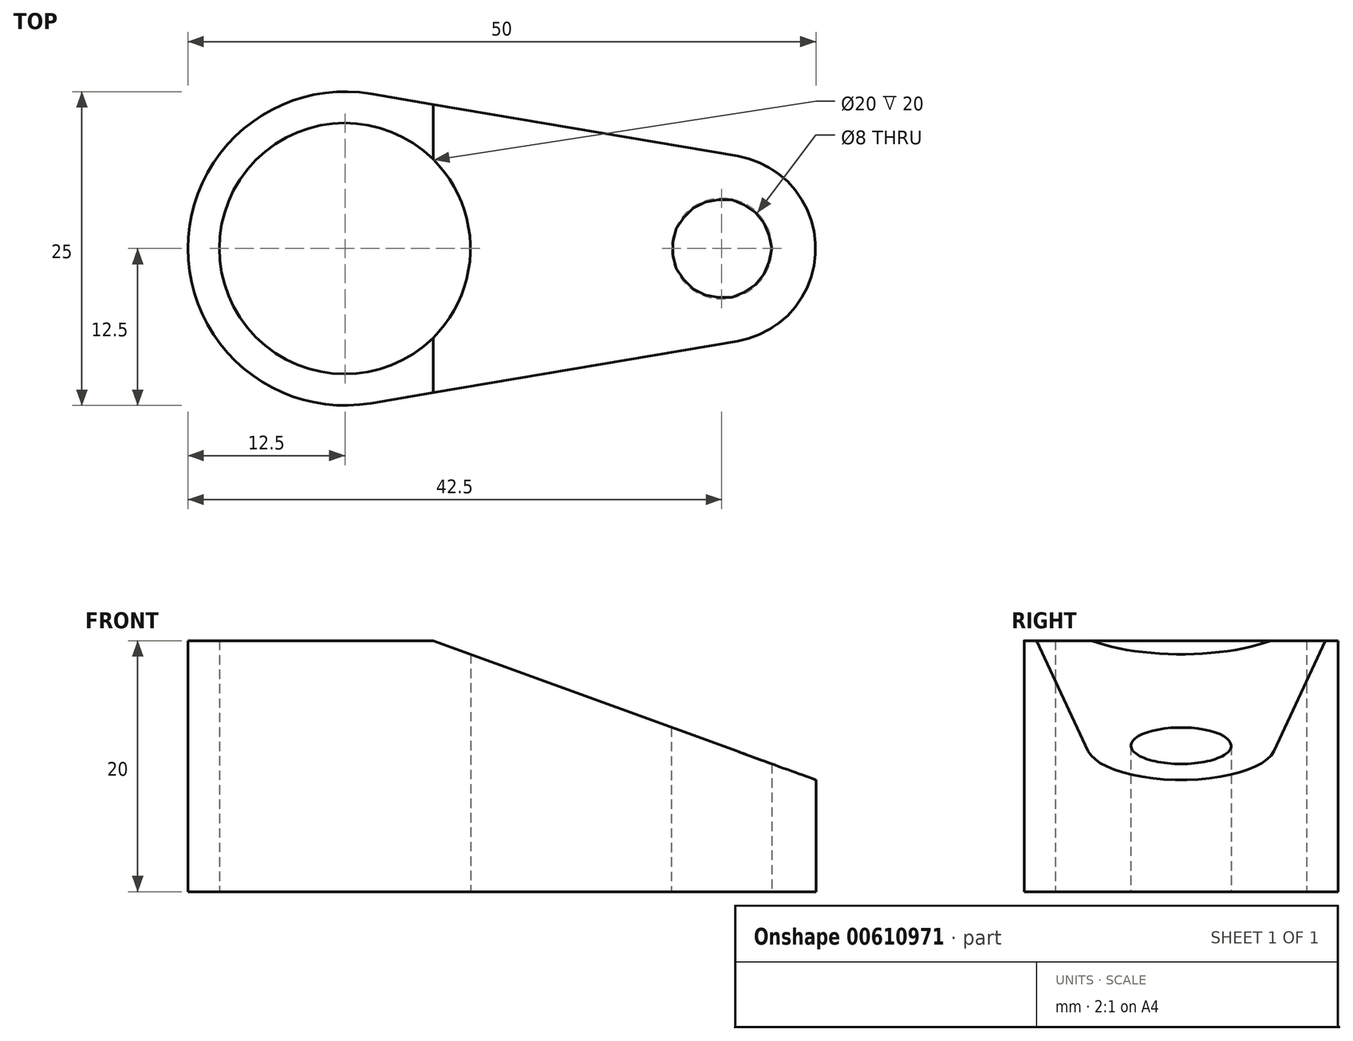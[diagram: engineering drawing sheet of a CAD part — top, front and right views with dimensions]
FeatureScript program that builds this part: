
annotation { "Feature Type Name" : "Feature", "Feature Type Description" : "" }
export const myFeature = defineFeature(function(context is Context, id is Id, definition is map)
    precondition{}
    {
        {
            var Q0;
            Q0=qCreatedBy(makeId("Top.planeOp"),FACE);
            var sketch = newSketch(context, id + "F0", { "sketchPlane" : qUnion([Q0])});
            skCircle(sketch, "E0", {"center": v(0, 0) * mm, "radius": 12.5 * mm});
            skCircle(sketch, "E1", {"center": v(30, 0) * mm, "radius": 7.5 * mm});
            skCircle(sketch, "E2", {"center": v(0, 0) * mm, "radius": 10 * mm});
            skCircle(sketch, "E3", {"center": v(30, 0) * mm, "radius": 4 * mm});
            skLineSegment(sketch, "E4", {"start": v(2.08, -12.33) * mm, "end": v(31.25, -7.4) * mm});
            skLineSegment(sketch, "E5", {"start": v(2.08, 12.33) * mm, "end": v(31.25, 7.4) * mm});
            skSolve(sketch);
        }
        {
            var Q0;
            Q0=makeQuery(id+"F0.imprint","IMPRINT",FACE,{"disambiguationData":[TD([[makeQuery(id+"F0.imprint","IMPRINT",EDGE,{"derivedFrom":sQuery(id+"F0.wireOp",EDGE,"E2")}),-1.0]])]});
            var Q1;
            Q1=makeQuery(id+"F0.imprint","IMPRINT",FACE,{"disambiguationData":[TD([[makeQuery(id+"F0.imprint","IMPRINT",EDGE,{"derivedFrom":sQuery(id+"F0.wireOp",EDGE,"E3")}),-1.0]])]});
            var Q2;
            {var subQ0=sQuery(id+"F0.wireOp",EDGE,"E4");Q2=makeQuery(id+"F0.imprint","IMPRINT",FACE,{"disambiguationData":[TD([[makeQuery(id+"F0.imprint","IMPRINT",EDGE,{"derivedFrom":subQ0}),1.0]])]});}
            extrude(context, id + "F1", {"entities" : qUnion([Q0, Q1, Q2]), "depth" : 20 * mm, "offsetDistance" : 25 * mm});
        }
        {
            var Q0;
            Q0=qCreatedBy(makeId("Front.planeOp"),FACE);
            var sketch = newSketch(context, id + "F2", { "sketchPlane" : qUnion([Q0])});
            skLineSegment(sketch, "E6", {"start": v(7.02, 20) * mm, "end": v(43.67, 20) * mm});
            skLineSegment(sketch, "E7", {"start": v(43.67, 20) * mm, "end": v(43.67, 6.66) * mm});
            skLineSegment(sketch, "E8", {"start": v(43.67, 6.66) * mm, "end": v(7.02, 20) * mm});
            skSolve(sketch);
        }
        {
            var Q0;
            Q0=makeQuery(id+"F2.imprint","IMPRINT",FACE,{"disambiguationData":[TD([[makeQuery(id+"F2.imprint","IMPRINT",EDGE,{"derivedFrom":sQuery(id+"F2.wireOp",EDGE,"E6")}),-1.0]])]});
            extrude(context, id + "F3", {"entities" : qUnion([Q0]), "operationType" : NewBodyOperationType.REMOVE, "endBound" : BoundingType.SYMMETRIC, "oppositeDirection" : true, "depth" : 25 * mm, "offsetDistance" : 25 * mm});
        }
    });
